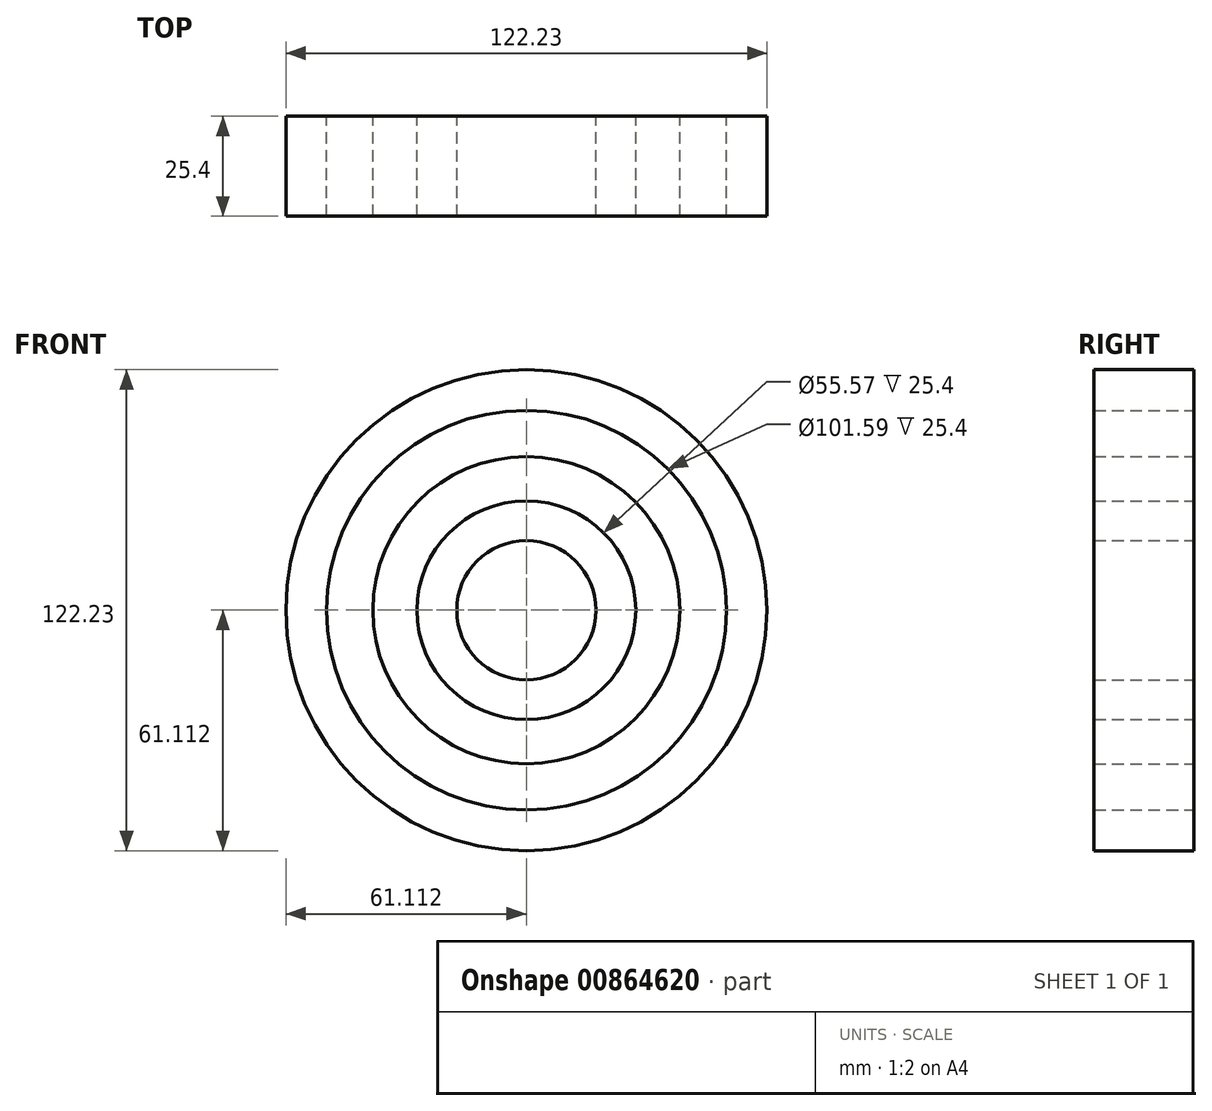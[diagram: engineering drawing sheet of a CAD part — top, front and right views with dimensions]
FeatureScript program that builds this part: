
annotation { "Feature Type Name" : "Feature", "Feature Type Description" : "" }
export const myFeature = defineFeature(function(context is Context, id is Id, definition is map)
    precondition{}
    {
        {
            var Q0;
            Q0=qCreatedBy(makeId("Front.planeOp"),FACE);
            var sketch = newSketch(context, id + "F0", { "sketchPlane" : qUnion([Q0])});
            skCircle(sketch, "E0", {"center": v(-42.04, 34.77) * mm, "radius": 17.68 * mm});
            skCircle(sketch, "E1.0", {"center": v(-42.04, 34.77) * mm, "radius": 39.01 * mm});
            skCircle(sketch, "E2.0", {"center": v(-42.04, 34.77) * mm, "radius": 27.79 * mm});
            skCircle(sketch, "E3.0", {"center": v(-42.04, 34.77) * mm, "radius": 50.8 * mm});
            skCircle(sketch, "E4.0", {"center": v(-42.04, 34.77) * mm, "radius": 61.12 * mm});
            skSolve(sketch);
        }
        {
            var Q0;
            Q0 = qSketchRegion(id + "F0", true);
            var Q1;
            Q1=makeQuery(id+"F0.imprint","IMPRINT",FACE,{"disambiguationData":[TD([[makeQuery(id+"F0.imprint","IMPRINT",EDGE,{"derivedFrom":sQuery(id+"F0.wireOp",EDGE,"E0")}),1.0]])]});
            var Q2;
            Q2=makeQuery(id+"F0.imprint","IMPRINT",FACE,{"disambiguationData":[TD([[makeQuery(id+"F0.imprint","IMPRINT",EDGE,{"derivedFrom":sQuery(id+"F0.wireOp",EDGE,"E1.0")}),1.0]])]});
            extrude(context, id + "F1", {"entities" : qUnion([Q0, Q1, Q2]), "depth" : 25.4 * mm, "offsetDistance" : 25.4 * mm});
        }
    });
